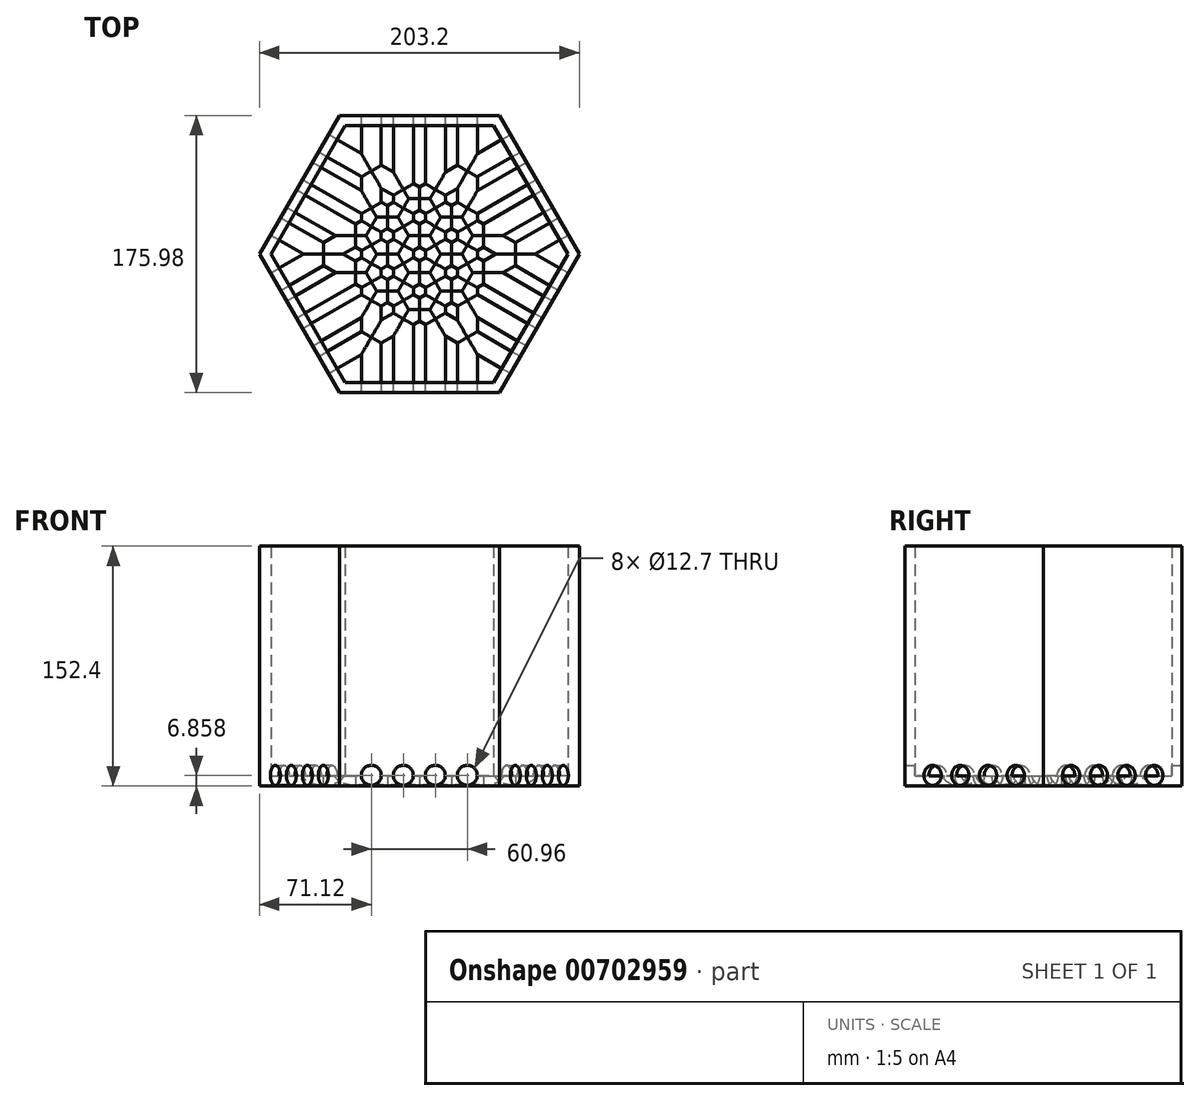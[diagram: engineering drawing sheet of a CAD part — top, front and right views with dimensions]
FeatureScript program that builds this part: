
annotation { "Feature Type Name" : "Feature", "Feature Type Description" : "" }
export const myFeature = defineFeature(function(context is Context, id is Id, definition is map)
    precondition{}
    {
        {
            var Q0;
            Q0=qCreatedBy(makeId("Top.planeOp"),FACE);
            var sketch = newSketch(context, id + "F0", { "sketchPlane" : qUnion([Q0])});
            skLineSegment(sketch, "E0", {"start": v(-101.6, 0) * mm, "end": v(-50.8, 87.99) * mm});
            skLineSegment(sketch, "E1", {"start": v(-50.8, 87.99) * mm, "end": v(50.8, 87.99) * mm});
            skLineSegment(sketch, "E2", {"start": v(50.8, 87.99) * mm, "end": v(101.6, 0) * mm});
            skLineSegment(sketch, "E3", {"start": v(101.6, 0) * mm, "end": v(50.8, -87.99) * mm});
            skLineSegment(sketch, "E4", {"start": v(50.8, -87.99) * mm, "end": v(-50.8, -87.99) * mm});
            skLineSegment(sketch, "E5", {"start": v(-50.8, -87.99) * mm, "end": v(-101.6, 0) * mm});
            skSolve(sketch);
        }
        {
            var Q0;
            Q0=qCreatedBy(makeId("Top.planeOp"),FACE);
            var sketch = newSketch(context, id + "F1", { "sketchPlane" : qUnion([Q0])});
            skLineSegment(sketch, "E6", {"start": v(-127, 0) * mm, "end": v(-63.5, 109.99) * mm});
            skLineSegment(sketch, "E7", {"start": v(-63.5, 109.99) * mm, "end": v(63.5, 109.99) * mm});
            skLineSegment(sketch, "E8", {"start": v(63.5, 109.99) * mm, "end": v(127, 0) * mm});
            skLineSegment(sketch, "E9", {"start": v(127, 0) * mm, "end": v(63.5, -109.99) * mm});
            skLineSegment(sketch, "E10", {"start": v(63.5, -109.99) * mm, "end": v(-63.5, -109.99) * mm});
            skLineSegment(sketch, "E11", {"start": v(-63.5, -109.99) * mm, "end": v(-127, 0) * mm});
            skLineSegment(sketch, "E12.0.0", {"start": v(-101.6, 0) * mm, "end": v(-50.8, -87.99) * mm});
            skLineSegment(sketch, "E12.0.1", {"start": v(-50.8, -87.99) * mm, "end": v(50.8, -87.99) * mm});
            skLineSegment(sketch, "E12.0.2", {"start": v(50.8, -87.99) * mm, "end": v(101.6, 0) * mm});
            skLineSegment(sketch, "E12.0.3", {"start": v(101.6, 0) * mm, "end": v(50.8, 87.99) * mm});
            skLineSegment(sketch, "E12.0.4", {"start": v(50.8, 87.99) * mm, "end": v(-50.8, 87.99) * mm});
            skLineSegment(sketch, "E12.0.5", {"start": v(-50.8, 87.99) * mm, "end": v(-101.6, 0) * mm});
            skSolve(sketch);
        }
        {
            var Q0;
            Q0=makeQuery(id+"F0.imprint","IMPRINT",FACE,{"disambiguationData":[TD([[makeQuery(id+"F0.imprint","IMPRINT",EDGE,{"derivedFrom":sQuery(id+"F0.wireOp",EDGE,"E0")}),-1.0]])]});
            extrude(context, id + "F2", {"entities" : qUnion([Q0]), "depth" : 152.4 * mm, "offsetDistance" : 25.4 * mm});
        }
        {
            var Q0;
            Q0=makeQuery(id+"F2.opExtrude","CAP_FACE",FACE,{"disambiguationData":[OSD([sQuery(id+"F0.wireOp",EDGE,"E0"),sQuery(id+"F0.wireOp",EDGE,"E1"),sQuery(id+"F0.wireOp",EDGE,"E2"),sQuery(id+"F0.wireOp",EDGE,"E3"),sQuery(id+"F0.wireOp",EDGE,"E4"),sQuery(id+"F0.wireOp",EDGE,"E5")])],"isStart":false});
            shell(context, id + "F3", {"entities" : qUnion([Q0]), "thickness" : 6.35 * mm});
        }
        {
            var Q0;
            Q0=makeQuery(id+"F2.opExtrude","SWEPT_FACE",FACE,{"disambiguationData":[OSD([sQuery(id+"F0.wireOp",EDGE,"E2")])]});
            var sketch = newSketch(context, id + "F4", { "sketchPlane" : qUnion([Q0])});
            skCircle(sketch, "E13", {"center": v(-30.48, 6.86) * mm, "radius": 6.35 * mm});
            skCircle(sketch, "E14", {"center": v(-10.16, 6.86) * mm, "radius": 6.35 * mm});
            skCircle(sketch, "E15", {"center": v(10.16, 6.86) * mm, "radius": 6.35 * mm});
            skCircle(sketch, "E16", {"center": v(30.48, 6.86) * mm, "radius": 6.35 * mm});
            skSolve(sketch);
        }
        {
            var Q0;
            Q0=makeQuery(id+"F4.imprint","IMPRINT",FACE,{"disambiguationData":[TD([[makeQuery(id+"F4.imprint","IMPRINT",EDGE,{"derivedFrom":sQuery(id+"F4.wireOp",EDGE,"E13")}),1.0]])]});
            var Q1;
            Q1=makeQuery(id+"F4.imprint","IMPRINT",FACE,{"disambiguationData":[TD([[makeQuery(id+"F4.imprint","IMPRINT",EDGE,{"derivedFrom":sQuery(id+"F4.wireOp",EDGE,"E14")}),1.0]])]});
            var Q2;
            Q2=makeQuery(id+"F4.imprint","IMPRINT",FACE,{"disambiguationData":[TD([[makeQuery(id+"F4.imprint","IMPRINT",EDGE,{"derivedFrom":sQuery(id+"F4.wireOp",EDGE,"E15")}),1.0]])]});
            var Q3;
            Q3=makeQuery(id+"F4.imprint","IMPRINT",FACE,{"disambiguationData":[TD([[makeQuery(id+"F4.imprint","IMPRINT",EDGE,{"derivedFrom":sQuery(id+"F4.wireOp",EDGE,"E16")}),1.0]])]});
            extrude(context, id + "F5", {"entities" : qUnion([Q0, Q1, Q2, Q3]), "operationType" : NewBodyOperationType.REMOVE, "oppositeDirection" : true, "depth" : 203.2 * mm, "offsetDistance" : 25.4 * mm});
        }
        {
            var Q0;
            Q0=makeQuery(id+"F2.opExtrude","SWEPT_FACE",FACE,{"disambiguationData":[OSD([sQuery(id+"F0.wireOp",EDGE,"E0")])]});
            var sketch = newSketch(context, id + "F6", { "sketchPlane" : qUnion([Q0])});
            skCircle(sketch, "E17", {"center": v(-30.48, 6.86) * mm, "radius": 6.35 * mm});
            skCircle(sketch, "E18", {"center": v(-10.16, 6.86) * mm, "radius": 6.35 * mm});
            skCircle(sketch, "E19", {"center": v(10.16, 6.86) * mm, "radius": 6.35 * mm});
            skCircle(sketch, "E20", {"center": v(30.48, 6.86) * mm, "radius": 6.35 * mm});
            skSolve(sketch);
        }
        {
            var Q0;
            Q0=makeQuery(id+"F6.imprint","IMPRINT",FACE,{"disambiguationData":[TD([[makeQuery(id+"F6.imprint","IMPRINT",EDGE,{"derivedFrom":sQuery(id+"F6.wireOp",EDGE,"E17")}),1.0]])]});
            var Q1;
            Q1=makeQuery(id+"F6.imprint","IMPRINT",FACE,{"disambiguationData":[TD([[makeQuery(id+"F6.imprint","IMPRINT",EDGE,{"derivedFrom":sQuery(id+"F6.wireOp",EDGE,"E18")}),1.0]])]});
            var Q2;
            Q2=makeQuery(id+"F6.imprint","IMPRINT",FACE,{"disambiguationData":[TD([[makeQuery(id+"F6.imprint","IMPRINT",EDGE,{"derivedFrom":sQuery(id+"F6.wireOp",EDGE,"E19")}),1.0]])]});
            var Q3;
            Q3=makeQuery(id+"F6.imprint","IMPRINT",FACE,{"disambiguationData":[TD([[makeQuery(id+"F6.imprint","IMPRINT",EDGE,{"derivedFrom":sQuery(id+"F6.wireOp",EDGE,"E20")}),1.0]])]});
            extrude(context, id + "F7", {"entities" : qUnion([Q0, Q1, Q2, Q3]), "operationType" : NewBodyOperationType.REMOVE, "oppositeDirection" : true, "depth" : 203.2 * mm, "offsetDistance" : 25.4 * mm});
        }
        {
            var Q0;
            Q0=makeQuery(id+"F2.opExtrude","SWEPT_FACE",FACE,{"disambiguationData":[OSD([sQuery(id+"F0.wireOp",EDGE,"E1")])]});
            var sketch = newSketch(context, id + "F8", { "sketchPlane" : qUnion([Q0])});
            skCircle(sketch, "E21", {"center": v(-30.48, 6.86) * mm, "radius": 6.35 * mm});
            skCircle(sketch, "E22", {"center": v(-10.16, 6.86) * mm, "radius": 6.35 * mm});
            skCircle(sketch, "E23", {"center": v(10.16, 6.86) * mm, "radius": 6.35 * mm});
            skCircle(sketch, "E24", {"center": v(30.48, 6.86) * mm, "radius": 6.35 * mm});
            skSolve(sketch);
        }
        {
            var Q0;
            Q0=makeQuery(id+"F8.imprint","IMPRINT",FACE,{"disambiguationData":[TD([[makeQuery(id+"F8.imprint","IMPRINT",EDGE,{"derivedFrom":sQuery(id+"F8.wireOp",EDGE,"E21")}),1.0]])]});
            var Q1;
            Q1=makeQuery(id+"F8.imprint","IMPRINT",FACE,{"disambiguationData":[TD([[makeQuery(id+"F8.imprint","IMPRINT",EDGE,{"derivedFrom":sQuery(id+"F8.wireOp",EDGE,"E22")}),1.0]])]});
            var Q2;
            Q2=makeQuery(id+"F8.imprint","IMPRINT",FACE,{"disambiguationData":[TD([[makeQuery(id+"F8.imprint","IMPRINT",EDGE,{"derivedFrom":sQuery(id+"F8.wireOp",EDGE,"E23")}),1.0]])]});
            var Q3;
            Q3=makeQuery(id+"F8.imprint","IMPRINT",FACE,{"disambiguationData":[TD([[makeQuery(id+"F8.imprint","IMPRINT",EDGE,{"derivedFrom":sQuery(id+"F8.wireOp",EDGE,"E24")}),1.0]])]});
            extrude(context, id + "F9", {"entities" : qUnion([Q0, Q1, Q2, Q3]), "operationType" : NewBodyOperationType.REMOVE, "oppositeDirection" : true, "depth" : 203.2 * mm, "offsetDistance" : 25.4 * mm});
        }
    });
